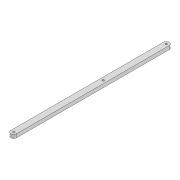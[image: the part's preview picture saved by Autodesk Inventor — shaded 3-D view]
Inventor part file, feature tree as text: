
AUTODESK INVENTOR PART (.ipt)
format: ipt  version: 2022 (Build 260153000, 153)  size: 90,624 bytes
history: native  units: mm
features: extrude x1, sketch x1
ambient origin geometry x8: Origin, YZ Plane, XZ Plane, XY Plane, X Axis, Y Axis, Z Axis, Center Point
bodies: Solid1 (feature_tree)
feature tree (2):
  extrude  "Extrusion1"  Depth=6.0mm
  sketch  "Sketch1"  dims[d0=3.3mm d1=3.3mm d2=10.0mm d3=261.6mm d4=3.3mm d5=153.559mm d6=6.0mm d7=0.0mm]
